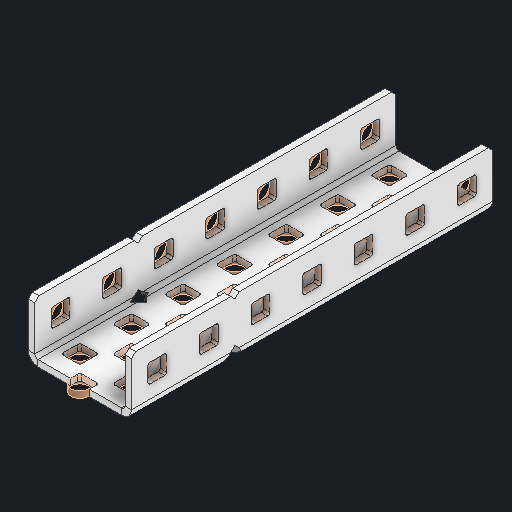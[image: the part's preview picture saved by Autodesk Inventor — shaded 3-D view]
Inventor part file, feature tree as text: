
AUTODESK INVENTOR PART (.ipt)
format: ipt  version: 2024 (Build 280153000, 153)  size: 738,304 bytes
history: native  units: in
note: dims shown in document units (in); Inventor stores cm internally (conversion verified against a paired STEP export)
features: other x76, sketch x5, sheet_metal_op x1
ambient origin geometry x8: Origin, YZ Plane, XZ Plane, XY Plane, X Axis, Y Axis, Z Axis, Center Point
bodies: Solid1 (feature_tree)
feature tree (82):
  other  "Alu C 1x2x1x7.ipt"
  other  "Solid1::Alu C 1x2x1x7.ipt"
  other  "TaggingFeature1"
  sketch  "Sketch1"  dims[d0=0.3937in]
  sketch  "Sketch2"  dims[d1=0.0625in]
  sketch  "Sketch3"
  other  "Flange Pattern Sketch"
  sketch  "Sketch9"
  sheet_metal_op  "Body Pattern Sketch"
  other  "Arc Length"
  sketch  "Sketch14"
  other  "Flange Pattern Plane"
  other  "Srf1"
  other  "Srf2"
  other  "Srf3"
  other  "Srf4"
  other  "Srf5"
  other  "Srf6"
  other  "Srf7"
  other  "Srf8"
  other  "Srf9"
  other  "Srf10"
  other  "Srf11"
  other  "Srf12"
  other  "Srf13"
  other  "Srf14"
  other  "Srf15"
  other  "Srf16"
  other  "Srf17"
  other  "Srf18"
  other  "Srf19"
  other  "Srf20"
  other  "Srf21"
  other  "Srf22"
  other  "Srf23"
  other  "Srf24"
  other  "Srf25"
  other  "Srf26"
  other  "Srf27"
  other  "Srf28"
  other  "Srf29"
  other  "Srf30"
  other  "Srf31"
  other  "Srf32"
  other  "Srf33"
  other  "Srf34"
  other  "Srf35"
  other  "Srf1::Derived"
  other  "Srf2::Derived"
  other  "Srf823::Derived"
  other  "Srf824::Derived"
  other  "Srf825::Derived"
  other  "Srf826::Derived"
  other  "Srf827::Derived"
  other  "Srf828::Derived"
  other  "Srf829::Derived"
  other  "Srf922::Derived"
  other  "Srf923::Derived"
  other  "Srf924::Derived"
  other  "Srf925::Derived"
  other  "Srf926::Derived"
  other  "Srf91::Derived"
  other  "Srf92::Derived"
  other  "Srf856::Derived"
  other  "Srf857::Derived"
  other  "Srf858::Derived"
  other  "Srf859::Derived"
  other  "Srf860::Derived"
  other  "Srf861::Derived"
  other  "Srf862::Derived"
  other  "Srf959::Derived"
  other  "Srf960::Derived"
  other  "Srf961::Derived"
  other  "Srf962::Derived"
  other  "Srf963::Derived"
  other  "Srf786::Derived"
  other  "Srf889::Derived"
  other  "Srf890::Derived"
  other  "Srf891::Derived"
  other  "Srf892::Derived"
  other  "Srf893::Derived"
  other  "Srf894::Derived"
